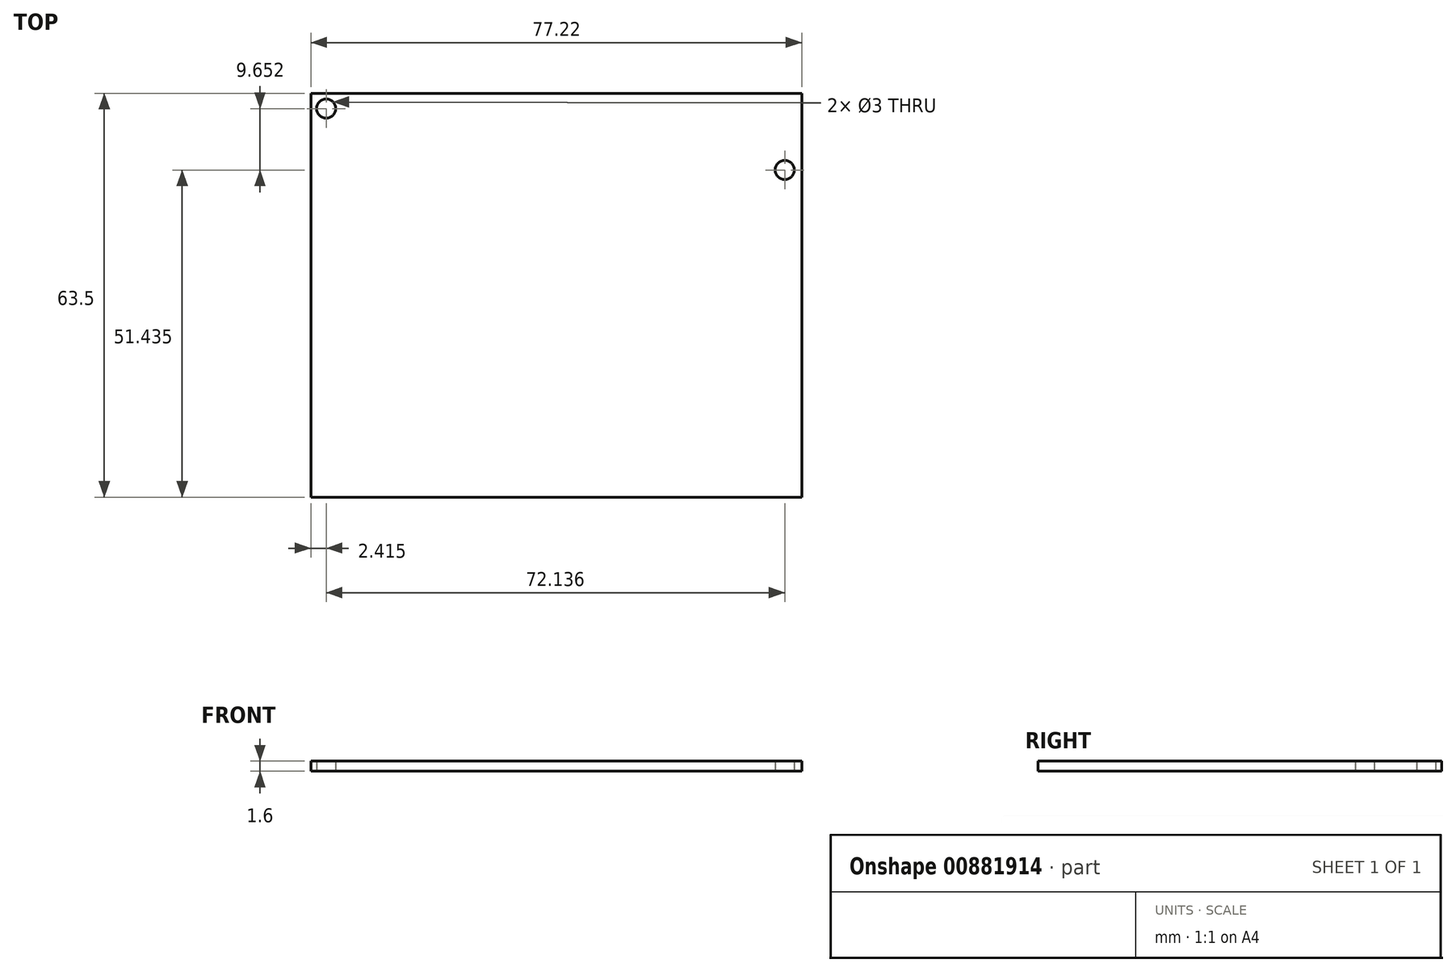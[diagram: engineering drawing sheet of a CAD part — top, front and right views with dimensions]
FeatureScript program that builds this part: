
annotation { "Feature Type Name" : "Feature", "Feature Type Description" : "" }
export const myFeature = defineFeature(function(context is Context, id is Id, definition is map)
    precondition{}
    {
        {
            var Q0;
            Q0=qCreatedBy(makeId("Top.planeOp"),FACE);
            var sketch = newSketch(context, id + "F0", { "sketchPlane" : qUnion([Q0])});
            skCircle(sketch, "E0.0", {"center": v(35.94, 19.68) * mm, "radius": 1.5 * mm});
            skCircle(sketch, "E1.0", {"center": v(-36.2, 29.34) * mm, "radius": 1.5 * mm});
            skPoint(sketch, "E2.0", {"position": v(-38.6, 31.75) * mm});
            skPoint(sketch, "E3.0", {"position": v(-38.6, -31.75) * mm});
            skPoint(sketch, "E4.0", {"position": v(38.6, -31.75) * mm});
            skPoint(sketch, "E5.0", {"position": v(38.6, 31.75) * mm});
            skLineSegment(sketch, "E6", {"start": v(-38.6, 31.75) * mm, "end": v(38.6, 31.75) * mm});
            skLineSegment(sketch, "E7", {"start": v(38.6, -31.75) * mm, "end": v(38.6, 31.75) * mm});
            skLineSegment(sketch, "E8", {"start": v(38.6, -31.75) * mm, "end": v(-38.6, -31.75) * mm});
            skLineSegment(sketch, "E9", {"start": v(-38.6, 31.75) * mm, "end": v(-38.6, -31.75) * mm});
            skPoint(sketch, "E10", {"position": v(0, 0) * mm});
            skPoint(sketch, "E10.positionSnap0", {"position": v(0, 31.75) * mm});
            skPoint(sketch, "E10.positionSnap1", {"position": v(38.6, 0) * mm});
            skLineSegment(sketch, "E11.bottom", {"start": v(-34.6, 9.75) * mm, "end": v(-27.6, 9.75) * mm, "construction": true});
            skLineSegment(sketch, "E11.top", {"start": v(-34.6, 1.75) * mm, "end": v(-27.6, 1.75) * mm, "construction": true});
            skLineSegment(sketch, "E11.left", {"start": v(-34.6, 9.75) * mm, "end": v(-34.6, 1.75) * mm, "construction": true});
            skLineSegment(sketch, "E11.right", {"start": v(-27.6, 9.75) * mm, "end": v(-27.6, 1.75) * mm, "construction": true});
            skSolve(sketch);
        }
        {
            var Q0;
            Q0=makeQuery(id+"F0.imprint","IMPRINT",FACE,{"disambiguationData":[TD([[makeQuery(id+"F0.imprint","IMPRINT",EDGE,{"derivedFrom":sQuery(id+"F0.wireOp",EDGE,"E0.0")}),-1.0]])]});
            extrude(context, id + "F1", {"entities" : qUnion([Q0]), "depth" : 1.6 * mm, "offsetDistance" : 25 * mm});
        }
    });
